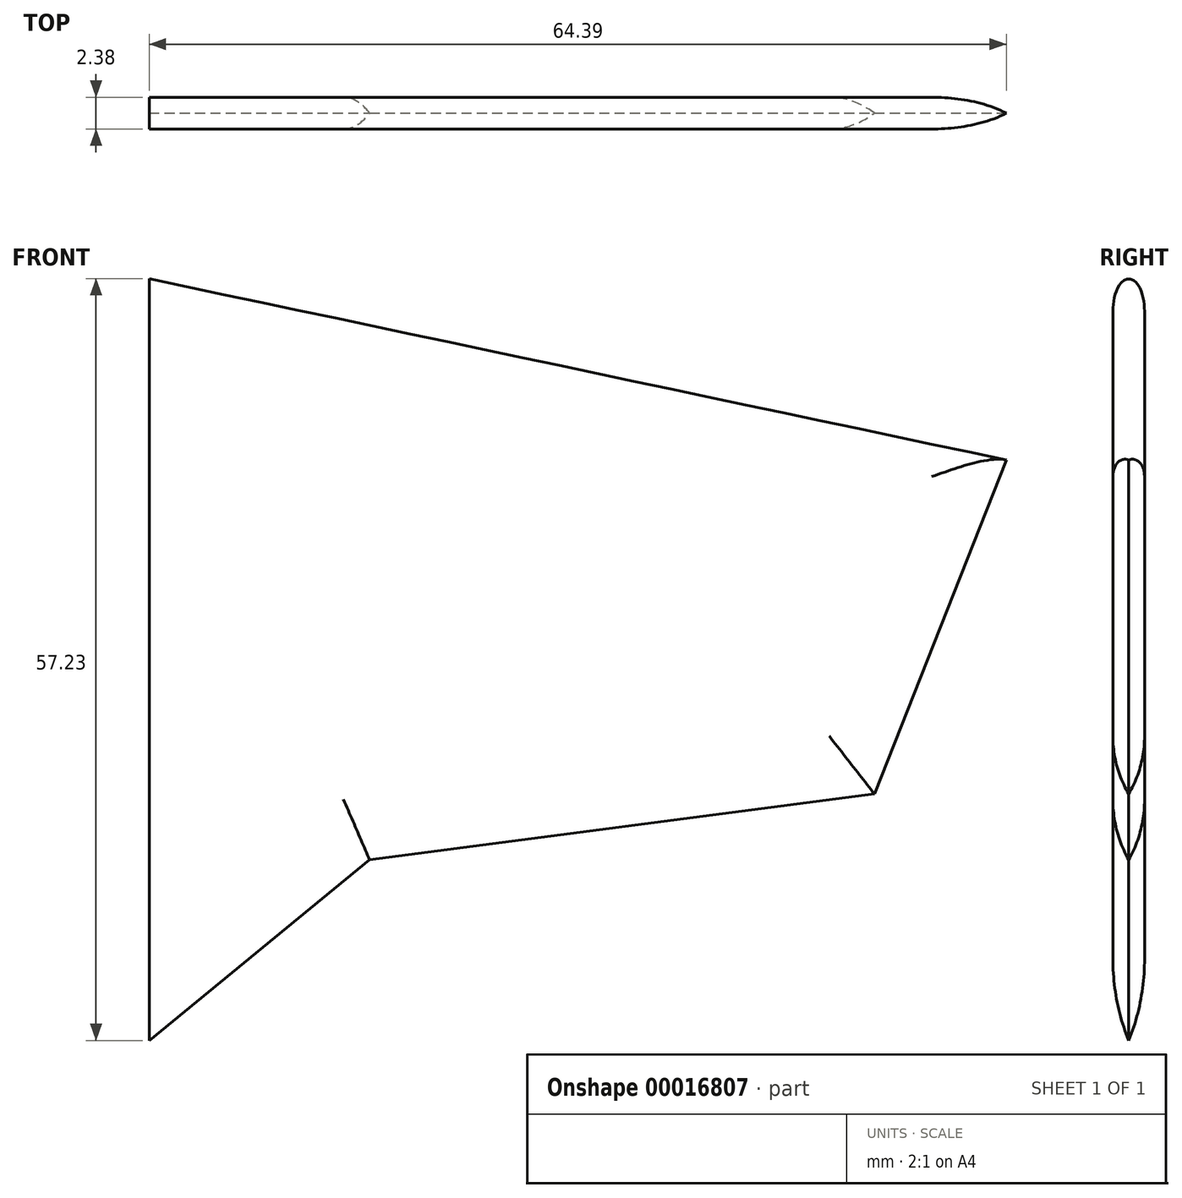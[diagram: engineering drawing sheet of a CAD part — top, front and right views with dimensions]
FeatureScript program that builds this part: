
annotation { "Feature Type Name" : "Feature", "Feature Type Description" : "" }
export const myFeature = defineFeature(function(context is Context, id is Id, definition is map)
    precondition{}
    {
        {
            var Q0;
            Q0=qCreatedBy(makeId("Front.planeOp"),FACE);
            var sketch = newSketch(context, id + "F0", { "sketchPlane" : qUnion([Q0])});
            skLineSegment(sketch, "E0", {"start": v(0, 0) * mm, "end": v(0, 57.23) * mm});
            skLineSegment(sketch, "E1", {"start": v(0, 57.23) * mm, "end": v(64.39, 43.61) * mm});
            skLineSegment(sketch, "E2", {"start": v(64.39, 43.61) * mm, "end": v(54.48, 18.52) * mm});
            skLineSegment(sketch, "E3", {"start": v(54.48, 18.52) * mm, "end": v(16.56, 13.56) * mm});
            skLineSegment(sketch, "E4", {"start": v(16.56, 13.56) * mm, "end": v(0, 0) * mm});
            skLineSegment(sketch, "E5", {"start": v(0, 57.23) * mm, "end": v(-12.1, 0) * mm, "construction": true});
            skLineSegment(sketch, "E6", {"start": v(-12.1, 0) * mm, "end": v(0, 0) * mm, "construction": true});
            skLineSegment(sketch, "E7", {"start": v(0, 0) * mm, "end": v(-9.62, 11.74) * mm, "construction": true});
            skSolve(sketch);
        }
        {
            var Q0;
            Q0=makeQuery(id+"F0.imprint","IMPRINT",FACE,{"disambiguationData":[TD([[makeQuery(id+"F0.imprint","IMPRINT",EDGE,{"derivedFrom":sQuery(id+"F0.wireOp",EDGE,"E0")}),-1.0]])]});
            extrude(context, id + "F1", {"entities" : qUnion([Q0]), "depth" : 2.38 * mm, "symmetric" : true});
        }
        {
            var Q0;
            Q0=qCreatedBy(makeId("Top.planeOp"),FACE);
            var sketch = newSketch(context, id + "F2", { "sketchPlane" : qUnion([Q0])});
            skLineSegment(sketch, "E8", {"start": v(-12.1, 25.4) * mm, "end": v(-12.1, -25.4) * mm});
            skLineSegment(sketch, "E9", {"start": v(-12.1, 25.4) * mm, "end": v(0, 25.4) * mm});
            skLineSegment(sketch, "E10", {"start": v(0, 25.4) * mm, "end": v(0, 0) * mm});
            skLineSegment(sketch, "E11", {"start": v(0, 0) * mm, "end": v(0, -25.4) * mm});
            skLineSegment(sketch, "E12", {"start": v(0, -25.4) * mm, "end": v(-12.1, -25.4) * mm});
            skSolve(sketch);
        }
        {
            var Q0;
            Q0=sQuery(id+"F0.wireOp",VERTEX,"E5.start");
            var Q1;
            Q1=sQuery(id+"F2.wireOp",VERTEX,"E8.end");
            var Q2;
            Q2=sQuery(id+"F2.wireOp",VERTEX,"E9.start");
            cPlane(context, id + "F3", {"entities" : qUnion([Q0, Q1, Q2]), "cplaneType" : CPlaneType.THREE_POINT, "offset" : 152.4 * mm, "width" : 152.4 * mm, "height" : 152.4 * mm});
        }
        {
            var Q0;
            Q0=qCreatedBy(id+"F3.planeOp",FACE);
            var sketch = newSketch(context, id + "F4", { "sketchPlane" : qUnion([Q0])});
            skLineSegment(sketch, "E13.0", {"start": v(1.2, 0) * mm, "end": v(1.2, 55.99) * mm, "construction": true});
            skLineSegment(sketch, "E14.0", {"start": v(-1.2, 0) * mm, "end": v(-1.2, 55.99) * mm, "construction": true});
            skLineSegment(sketch, "E15.0", {"start": v(1.2, 55.99) * mm, "end": v(-1.2, 55.99) * mm, "construction": true});
            skLineSegment(sketch, "E16", {"start": v(-1.2, 53.6) * mm, "end": v(1.2, 53.6) * mm, "construction": true});
            skLineSegment(sketch, "E17", {"start": v(0, 55.99) * mm, "end": v(0, 53.6) * mm, "construction": true});
            skEllipticalArc(sketch, "E18", {});
            skLineSegment(sketch, "E19", {"start": v(-1.2, 53.6) * mm, "end": v(-12.7, 53.6) * mm});
            skLineSegment(sketch, "E20", {"start": v(-12.7, 53.6) * mm, "end": v(-12.7, 68.69) * mm});
            skLineSegment(sketch, "E21", {"start": v(-12.7, 68.69) * mm, "end": v(12.7, 68.69) * mm});
            skLineSegment(sketch, "E22", {"start": v(12.7, 68.69) * mm, "end": v(12.7, 53.6) * mm});
            skLineSegment(sketch, "E23", {"start": v(12.7, 53.6) * mm, "end": v(1.2, 53.6) * mm});
            const initialGuessF4  = {"E18": [0, 0.05360710351963135, 0, 1, 0.0023812500000000014, 0.0011906249999999998, 4.71238898038469, 1.5707963267948972]};
            skSetInitialGuess(sketch, initialGuessF4);
            skSolve(sketch);
        }
        {
            var Q0;
            Q0 = qSketchRegion(id + "F4", true);
            extrude(context, id + "F5", {"entities" : qUnion([Q0]), "operationType" : NewBodyOperationType.REMOVE, "endBound" : BoundingType.THROUGH_ALL, "oppositeDirection" : true, "depth" : 25.4 * mm});
        }
        {
            var Q0;
            Q0=sQuery(id+"F0.wireOp",VERTEX,"E7.end");
            var Q1;
            Q1=sQuery(id+"F2.wireOp",VERTEX,"E12.start");
            var Q2;
            Q2=sQuery(id+"F2.wireOp",VERTEX,"E10.start");
            cPlane(context, id + "F6", {"entities" : qUnion([Q0, Q1, Q2]), "cplaneType" : CPlaneType.THREE_POINT, "offset" : 152.4 * mm, "width" : 152.4 * mm, "height" : 152.4 * mm});
        }
        {
            var Q0;
            Q0=qCreatedBy(id+"F6.planeOp",FACE);
            var sketch = newSketch(context, id + "F7", { "sketchPlane" : qUnion([Q0])});
            skLineSegment(sketch, "E24.0", {"start": v(1.2, 4.76) * mm, "end": v(1.2, 42.39) * mm, "construction": true});
            skLineSegment(sketch, "E25.0", {"start": v(-1.2, 0) * mm, "end": v(-1.2, 42.39) * mm, "construction": true});
            skLineSegment(sketch, "E26", {"start": v(1.2, 0) * mm, "end": v(-1.2, 0) * mm});
            skLineSegment(sketch, "E27", {"start": v(1.2, 4.76) * mm, "end": v(-1.2, 4.76) * mm, "construction": true});
            skArc(sketch, "E28", {"start": v(1.2, 4.76) * mm, "mid": v(0.89, 2.3) * mm, "end": v(0, 0) * mm});
            skArc(sketch, "E29.MirrorCS", {"start": v(-1.2, 4.76) * mm, "mid": v(-0.89, 2.3) * mm, "end": v(0, 0) * mm});
            skLineSegment(sketch, "E30", {"start": v(1.2, 4.76) * mm, "end": v(12.7, 4.76) * mm});
            skLineSegment(sketch, "E31", {"start": v(12.7, 4.76) * mm, "end": v(12.7, -12.7) * mm});
            skLineSegment(sketch, "E32", {"start": v(12.7, -12.7) * mm, "end": v(-12.7, -12.7) * mm});
            skLineSegment(sketch, "E33", {"start": v(-12.7, -12.7) * mm, "end": v(-12.7, 4.76) * mm});
            skLineSegment(sketch, "E34", {"start": v(-12.7, 4.76) * mm, "end": v(-1.2, 4.76) * mm});
            skSolve(sketch);
        }
        {
            var Q0;
            Q0 = qSketchRegion(id + "F7", true);
            var Q1;
            Q1=sQuery(id+"F0.wireOp",EDGE,"E4");
            var Q2;
            Q2=sQuery(id+"F0.wireOp",EDGE,"E3");
            var Q3;
            Q3=sQuery(id+"F0.wireOp",EDGE,"E2");
            sweep(context, id + "F8", {"operationType" : NewBodyOperationType.REMOVE, "profiles" : qUnion([Q0]), "path" : qUnion([Q1, Q2, Q3])});
        }
    });
